# Revit family: 8474545440 virtu comfort grab rail 450x450mm LH 90 vertical
name_source: partatom
category: Plumbing Fixtures
revit_build: Autodesk Revit 2015 (Build: 20140606_1530(x64)
units: mm (PartAtom-declared; Revit-internal decimal feet)

## types (1)
- Virtu Comfort Grab Rail 450x450mm LH 90° Vertical
    Assembly Code = C1030200
    CW Connection = No
    Default Elevation = 0 mm  [stored 0 ft]
    Description = Virtu Comfort Grab Rail 450x450mm LH 90° Vertical
    HW Connection = No
    Manufacturer = GWA Bathrooms & Kitchens
    Material_Base = GWA_Metal-Stainless
    Model = 8474545440
    Rail_Height = 73 mm  [stored 0.239501 ft]
    Rail_Width = 450 mm  [stored 1.47638 ft]
    URL = https://www.caroma.com.au
    Vent Connection = No
    Waste Connection = No

note: [stored X ft] marks values corroborated as IEEE doubles in the binary element streams (Revit-internal decimal feet)

## geometry (parser evidence)
native form markers: Sweep x2
no freeform markers — native parametric forms only
